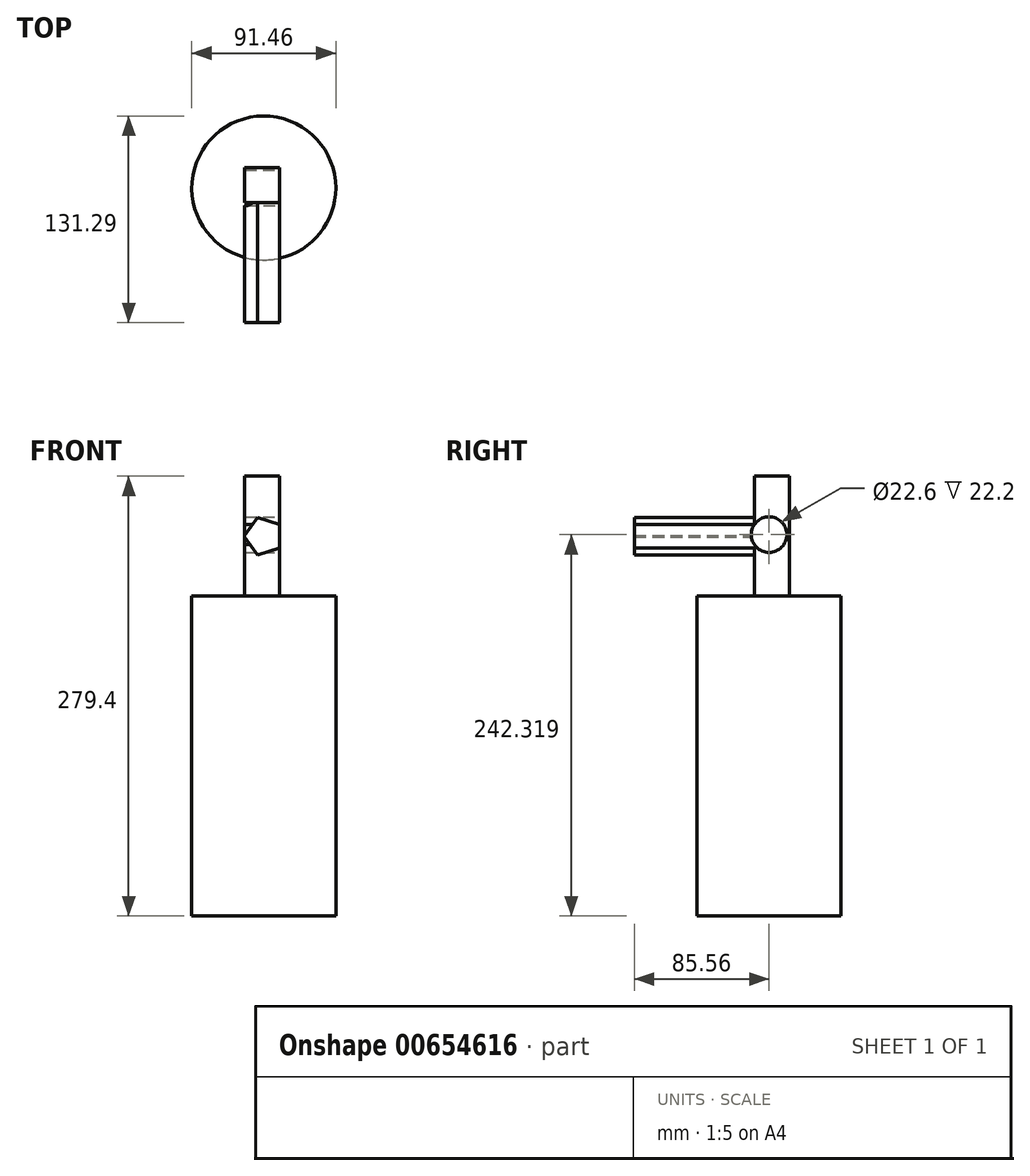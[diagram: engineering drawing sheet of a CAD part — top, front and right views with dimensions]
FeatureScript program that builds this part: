
annotation { "Feature Type Name" : "Feature", "Feature Type Description" : "" }
export const myFeature = defineFeature(function(context is Context, id is Id, definition is map)
    precondition{}
    {
        {
            var Q0;
            Q0=qCreatedBy(makeId("Top.planeOp"),FACE);
            var sketch = newSketch(context, id + "F0", { "sketchPlane" : qUnion([Q0])});
            skCircle(sketch, "E0", {"center": v(0, 0) * mm, "radius": 45.73 * mm});
            skSolve(sketch);
        }
        {
            var Q0;
            Q0=makeQuery(id+"F0.imprint","IMPRINT",FACE,{"disambiguationData":[TD([[makeQuery(id+"F0.imprint","IMPRINT",EDGE,{"derivedFrom":sQuery(id+"F0.wireOp",EDGE,"E0")}),1.0]])]});
            extrude(context, id + "F1", {"entities" : qUnion([Q0]), "depth" : 203.2 * mm, "offsetDistance" : 25.4 * mm});
        }
        {
            var Q0;
            Q0=makeQuery(id+"F1.opExtrude","CAP_FACE",FACE,{"disambiguationData":[OSD([sQuery(id+"F0.wireOp",EDGE,"E0")])],"isStart":false});
            var sketch = newSketch(context, id + "F2", { "sketchPlane" : qUnion([Q0])});
            skLineSegment(sketch, "E1.bottom", {"start": v(-12.09, -9.36) * mm, "end": v(10.11, -9.36) * mm});
            skLineSegment(sketch, "E1.top", {"start": v(-12.09, 12.84) * mm, "end": v(10.11, 12.84) * mm});
            skLineSegment(sketch, "E1.left", {"start": v(-12.09, -9.36) * mm, "end": v(-12.09, 12.84) * mm});
            skLineSegment(sketch, "E1.right", {"start": v(10.11, -9.36) * mm, "end": v(10.11, 12.84) * mm});
            skSolve(sketch);
        }
        {
            var Q0;
            Q0=makeQuery(id+"F2.imprint","IMPRINT",FACE,{"disambiguationData":[TD([[makeQuery(id+"F2.imprint","IMPRINT",EDGE,{"derivedFrom":sQuery(id+"F2.wireOp",EDGE,"E1.bottom")}),1.0]])]});
            extrude(context, id + "F3", {"entities" : qUnion([Q0]), "operationType" : NewBodyOperationType.ADD, "depth" : 76.2 * mm, "offsetDistance" : 25.4 * mm});
        }
        {
            var Q0;
            Q0=makeQuery(id+"F3.opExtrude","SWEPT_FACE",FACE,{"disambiguationData":[OSD([sQuery(id+"F2.wireOp",EDGE,"E1.bottom")])]});
            var sketch = newSketch(context, id + "F4", { "sketchPlane" : qUnion([Q0])});
            skCircle(sketch, "E2.cCircle", {"center": v(0, 241.3) * mm, "radius": 10.11 * mm, "construction": true});
            skPoint(sketch, "E2.cCircle.centerSnap0", {"position": v(10.11, 241.3) * mm});
            skLineSegment(sketch, "E2.0", {"start": v(10.11, 248.65) * mm, "end": v(10.11, 233.95) * mm});
            skLineSegment(sketch, "E2.1", {"start": v(10.11, 233.95) * mm, "end": v(-3.86, 229.41) * mm});
            skLineSegment(sketch, "E2.2", {"start": v(-3.86, 229.41) * mm, "end": v(-12.5, 241.3) * mm});
            skLineSegment(sketch, "E2.3", {"start": v(-12.5, 241.3) * mm, "end": v(-3.86, 253.19) * mm});
            skLineSegment(sketch, "E2.4", {"start": v(-3.86, 253.19) * mm, "end": v(10.11, 248.65) * mm});
            skPoint(sketch, "E2.0.midPoint", {"position": v(10.11, 241.3) * mm});
            skSolve(sketch);
        }
        {
            var Q0;
            Q0=makeQuery(id+"F4.imprint","IMPRINT",FACE,{"disambiguationData":[TD([[makeQuery(id+"F4.imprint","IMPRINT",EDGE,{"derivedFrom":sQuery(id+"F4.wireOp",EDGE,"E2.0")}),-1.0]])]});
            extrude(context, id + "F5", {"entities" : qUnion([Q0]), "operationType" : NewBodyOperationType.ADD, "depth" : 76.2 * mm, "offsetDistance" : 25.4 * mm});
        }
        {
            var Q0;
            Q0=makeQuery(id+"F5.boolean.opBoolean","MERGE",FACE,{"derivedFrom":[makeQuery(id+"F3.opExtrude","SWEPT_FACE",FACE,{"disambiguationData":[OSD([sQuery(id+"F2.wireOp",EDGE,"E1.right")])]}),makeQuery(id+"F5.opExtrude","SWEPT_FACE",FACE,{"disambiguationData":[OSD([sQuery(id+"F4.wireOp",EDGE,"E2.0")])]})]});
            var sketch = newSketch(context, id + "F6", { "sketchPlane" : qUnion([Q0])});
            skCircle(sketch, "E3", {"center": v(0, 242.32) * mm, "radius": 11.3 * mm});
            skSolve(sketch);
        }
        {
            var Q0;
            Q0=makeQuery(id+"F6.imprint","IMPRINT",FACE,{"disambiguationData":[TD([[makeQuery(id+"F6.imprint","IMPRINT",EDGE,{"derivedFrom":sQuery(id+"F6.wireOp",EDGE,"E3")}),1.0]])]});
            var Q1;
            Q1=sQuery(id+"F6.wireOp",EDGE,"E3");
            extrude(context, id + "F7", {"entities" : qUnion([Q0]), "operationType" : NewBodyOperationType.REMOVE, "surfaceEntities" : qUnion([Q1]), "oppositeDirection" : true, "depth" : 25.4 * mm, "offsetDistance" : 25.4 * mm});
        }
    });
